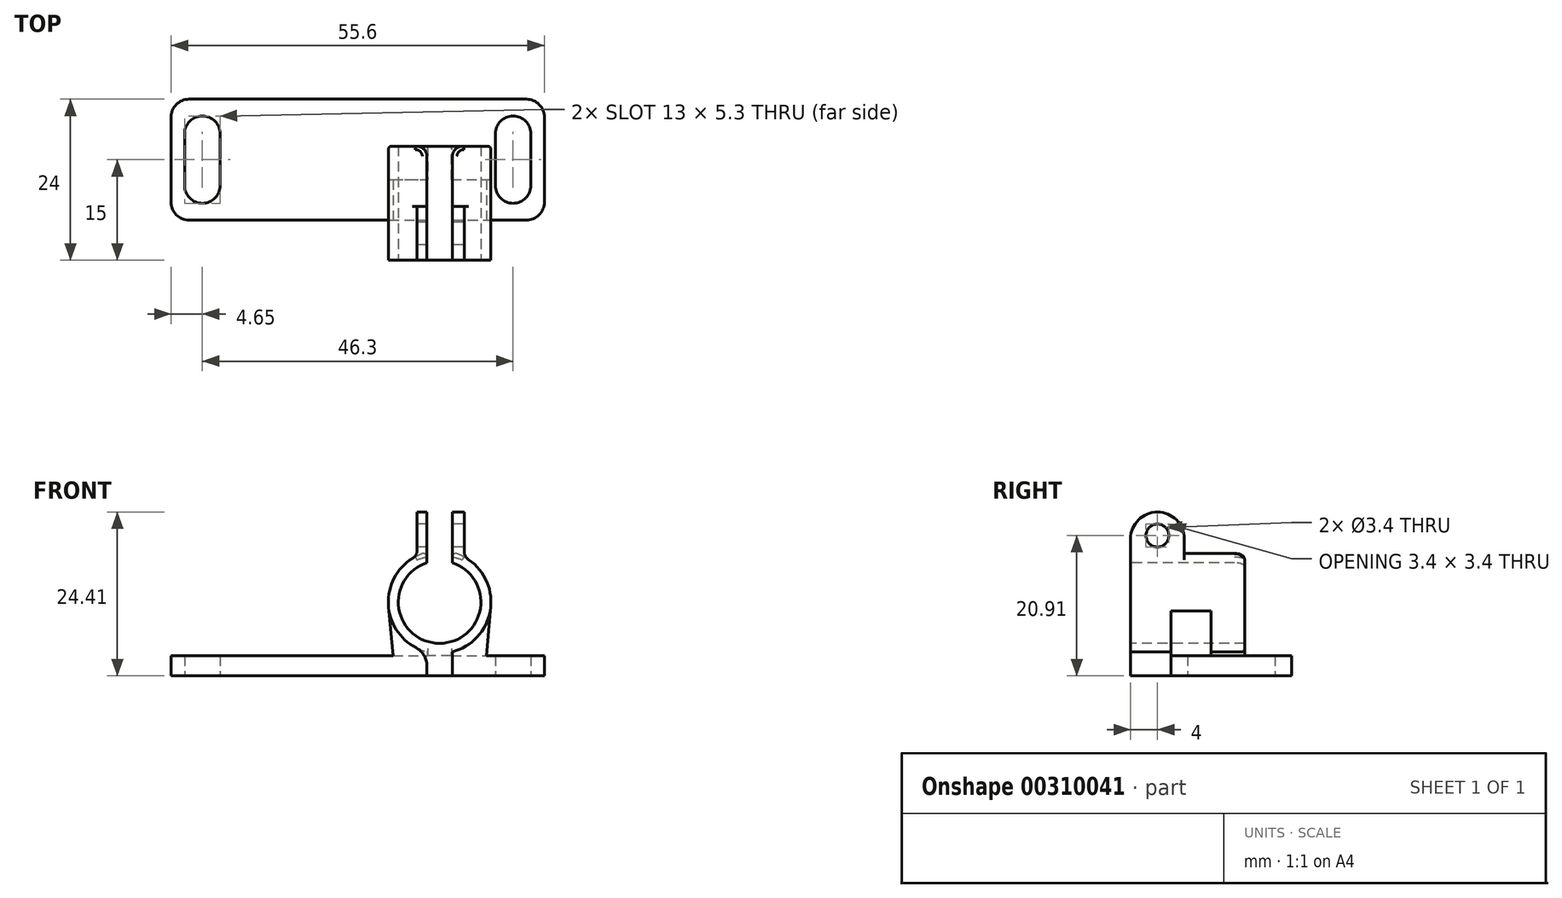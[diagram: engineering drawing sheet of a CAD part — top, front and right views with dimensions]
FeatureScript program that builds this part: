
annotation { "Feature Type Name" : "Feature", "Feature Type Description" : "" }
export const myFeature = defineFeature(function(context is Context, id is Id, definition is map)
    precondition{}
    {
        {
            var Q0;
            Q0=qCreatedBy(makeId("Top.planeOp"),FACE);
            var sketch = newSketch(context, id + "F0", { "sketchPlane" : qUnion([Q0])});
            skLineSegment(sketch, "E0.bottom", {"start": v(2.65, 0) * mm, "end": v(2.65, 0) * mm});
            skLineSegment(sketch, "E0.top", {"start": v(2.65, 13) * mm, "end": v(2.65, 13) * mm});
            skLineSegment(sketch, "E0.left", {"start": v(0, 2.65) * mm, "end": v(0, 10.35) * mm});
            skLineSegment(sketch, "E0.right", {"start": v(5.3, 2.65) * mm, "end": v(5.3, 10.35) * mm});
            skLineSegment(sketch, "E1.bottom", {"start": v(48.95, 0) * mm, "end": v(48.95, 0) * mm});
            skLineSegment(sketch, "E1.top", {"start": v(48.95, 13) * mm, "end": v(48.95, 13) * mm});
            skLineSegment(sketch, "E1.left", {"start": v(46.3, 2.65) * mm, "end": v(46.3, 10.35) * mm});
            skLineSegment(sketch, "E1.right", {"start": v(51.6, 2.65) * mm, "end": v(51.6, 10.35) * mm});
            skPoint(sketch, "E2.visualSharp", {"position": v(0, 13) * mm});
            skArc(sketch, "E2.filletArc", {"start": v(2.65, 13) * mm, "mid": v(0.78, 12.22) * mm, "end": v(0, 10.35) * mm});
            skPoint(sketch, "E3.visualSharp", {"position": v(5.3, 13) * mm});
            skArc(sketch, "E3.filletArc", {"start": v(5.3, 10.35) * mm, "mid": v(4.52, 12.22) * mm, "end": v(2.65, 13) * mm});
            skPoint(sketch, "E4.visualSharp", {"position": v(0, 0) * mm});
            skArc(sketch, "E4.filletArc", {"start": v(0, 2.65) * mm, "mid": v(0.78, 0.78) * mm, "end": v(2.65, 0) * mm});
            skPoint(sketch, "E5.visualSharp", {"position": v(5.3, 0) * mm});
            skArc(sketch, "E5.filletArc", {"start": v(2.65, 0) * mm, "mid": v(4.52, 0.78) * mm, "end": v(5.3, 2.65) * mm});
            skPoint(sketch, "E6.visualSharp", {"position": v(46.3, 13) * mm});
            skArc(sketch, "E6.filletArc", {"start": v(48.95, 13) * mm, "mid": v(47.08, 12.22) * mm, "end": v(46.3, 10.35) * mm});
            skPoint(sketch, "E7.visualSharp", {"position": v(51.6, 13) * mm});
            skArc(sketch, "E7.filletArc", {"start": v(51.6, 10.35) * mm, "mid": v(50.82, 12.22) * mm, "end": v(48.95, 13) * mm});
            skPoint(sketch, "E8.visualSharp", {"position": v(51.6, 0) * mm});
            skArc(sketch, "E8.filletArc", {"start": v(48.95, 0) * mm, "mid": v(50.82, 0.78) * mm, "end": v(51.6, 2.65) * mm});
            skPoint(sketch, "E9.visualSharp", {"position": v(46.3, 0) * mm});
            skArc(sketch, "E9.filletArc", {"start": v(46.3, 2.65) * mm, "mid": v(47.08, 0.78) * mm, "end": v(48.95, 0) * mm});
            skLineSegment(sketch, "E10.bottom", {"start": v(0.65, -2.5) * mm, "end": v(50.95, -2.5) * mm});
            skLineSegment(sketch, "E10.top", {"start": v(0.65, 15.5) * mm, "end": v(50.95, 15.5) * mm});
            skLineSegment(sketch, "E10.left", {"start": v(-2, 0.15) * mm, "end": v(-2, 12.85) * mm});
            skLineSegment(sketch, "E10.right", {"start": v(53.6, 0.15) * mm, "end": v(53.6, 12.85) * mm});
            skPoint(sketch, "E11.visualSharp", {"position": v(-2, 15.5) * mm});
            skArc(sketch, "E11.filletArc", {"start": v(0.65, 15.5) * mm, "mid": v(-1.22, 14.72) * mm, "end": v(-2, 12.85) * mm});
            skPoint(sketch, "E12.visualSharp", {"position": v(53.6, 15.5) * mm});
            skArc(sketch, "E12.filletArc", {"start": v(53.6, 12.85) * mm, "mid": v(52.82, 14.72) * mm, "end": v(50.95, 15.5) * mm});
            skPoint(sketch, "E13.visualSharp", {"position": v(53.6, -2.5) * mm});
            skArc(sketch, "E13.filletArc", {"start": v(50.95, -2.5) * mm, "mid": v(52.82, -1.72) * mm, "end": v(53.6, 0.15) * mm});
            skPoint(sketch, "E14.visualSharp", {"position": v(-2, -2.5) * mm});
            skArc(sketch, "E14.filletArc", {"start": v(-2, 0.15) * mm, "mid": v(-1.22, -1.72) * mm, "end": v(0.65, -2.5) * mm});
            skSolve(sketch);
        }
        {
            var Q0;
            Q0=makeQuery(id+"F0.imprint","IMPRINT",FACE,{"disambiguationData":[TD([[makeQuery(id+"F0.imprint","IMPRINT",EDGE,{"derivedFrom":sQuery(id+"F0.wireOp",EDGE,"E0.left")}),1.0]])]});
            extrude(context, id + "F1", {"entities" : qUnion([Q0]), "depth" : 3 * mm});
        }
        {
            var Q0;
            Q0=qCreatedBy(makeId("Front.planeOp"),FACE);
            var sketch = newSketch(context, id + "F2", { "sketchPlane" : qUnion([Q0])});
            skArc(sketch, "E15", {"start": v(36.1, 16.85) * mm, "mid": v(38, 4.85) * mm, "end": v(39.9, 16.85) * mm});
            skArc(sketch, "E16", {"start": v(36.1, 18.41) * mm, "mid": v(38, 3.35) * mm, "end": v(39.9, 18.41) * mm});
            skLineSegment(sketch, "E17", {"start": v(39.9, 18.41) * mm, "end": v(39.9, 16.85) * mm});
            skLineSegment(sketch, "E18", {"start": v(36.1, 18.41) * mm, "end": v(36.1, 16.85) * mm});
            skSolve(sketch);
        }
        {
            var Q0;
            Q0=makeQuery(id+"F2.imprint","IMPRINT",FACE,{"disambiguationData":[TD([[makeQuery(id+"F2.imprint","IMPRINT",EDGE,{"derivedFrom":sQuery(id+"F2.wireOp",EDGE,"E15")}),-1.0]])]});
            extrude(context, id + "F3", {"entities" : qUnion([Q0]), "endBound" : BoundingType.SYMMETRIC, "oppositeDirection" : true, "depth" : 17 * mm});
        }
        {
            var Q0;
            Q0=makeQuery(id+"F1.opExtrude","SWEPT_FACE",FACE,{"disambiguationData":[OSD([sQuery(id+"F0.wireOp",EDGE,"E10.bottom")])]});
            var sketch = newSketch(context, id + "F4", { "sketchPlane" : qUnion([Q0])});
            skArc(sketch, "E19", {"start": v(30.35, 11) * mm, "mid": v(38, 3.35) * mm, "end": v(45.65, 11) * mm});
            skLineSegment(sketch, "E20", {"start": v(30.35, 11) * mm, "end": v(31.05, 3) * mm});
            skLineSegment(sketch, "E21", {"start": v(31.05, 3) * mm, "end": v(44.95, 3) * mm});
            skLineSegment(sketch, "E22", {"start": v(44.95, 3) * mm, "end": v(45.65, 11) * mm});
            skSolve(sketch);
        }
        {
            var Q0;
            Q0=makeQuery(id+"F4.imprint","IMPRINT",FACE,{"disambiguationData":[TD([[makeQuery(id+"F4.imprint","IMPRINT",EDGE,{"derivedFrom":sQuery(id+"F4.wireOp",EDGE,"E19")}),-1.0]])]});
            extrude(context, id + "F5", {"entities" : qUnion([Q0]), "operationType" : NewBodyOperationType.ADD, "oppositeDirection" : true, "depth" : 6 * mm});
        }
        {
            var Q0;
            Q0=makeQuery(id+"F3.opExtrude","CAP_FACE",FACE,{"disambiguationData":[OSD([sQuery(id+"F2.wireOp",EDGE,"E15"),sQuery(id+"F2.wireOp",EDGE,"E16"),sQuery(id+"F2.wireOp",EDGE,"E17"),sQuery(id+"F2.wireOp",EDGE,"E18")])],"isStart":false});
            var sketch = newSketch(context, id + "F6", { "sketchPlane" : qUnion([Q0])});
            skLineSegment(sketch, "E23", {"start": v(-39.75, 3.7) * mm, "end": v(-39.75, 0) * mm});
            skLineSegment(sketch, "E24", {"start": v(-39.75, 0) * mm, "end": v(-36.1, 0) * mm});
            skLineSegment(sketch, "E25", {"start": v(-36.1, 0) * mm, "end": v(-36.25, 3.7) * mm});
            skArc(sketch, "E26", {"start": v(-39.75, 3.7) * mm, "mid": v(-38, 3.5) * mm, "end": v(-36.25, 3.7) * mm});
            skSolve(sketch);
        }
        {
            var Q0;
            {var subQ0=sQuery(id+"F6.wireOp",EDGE,"E24");Q0=makeQuery(id+"F6.imprint","IMPRINT",FACE,{"disambiguationData":[TD([[makeQuery(id+"F6.imprint","IMPRINT",EDGE,{"derivedFrom":subQ0}),1.0]])]});}
            extrude(context, id + "F7", {"entities" : qUnion([Q0]), "operationType" : NewBodyOperationType.ADD, "oppositeDirection" : true, "depth" : 10 * mm});
        }
        {
            var Q0;
            Q0=makeQuery(id+"F3.opExtrude","CAP_FACE",FACE,{"disambiguationData":[OSD([sQuery(id+"F2.wireOp",EDGE,"E15"),sQuery(id+"F2.wireOp",EDGE,"E16"),sQuery(id+"F2.wireOp",EDGE,"E17"),sQuery(id+"F2.wireOp",EDGE,"E18")])],"isStart":true});
            var sketch = newSketch(context, id + "F8", { "sketchPlane" : qUnion([Q0])});
            skLineSegment(sketch, "E27", {"start": v(36.1, 3.59) * mm, "end": v(36.1, 0) * mm});
            skLineSegment(sketch, "E28", {"start": v(36.1, 0) * mm, "end": v(39.9, 0) * mm});
            skLineSegment(sketch, "E29", {"start": v(39.9, 0) * mm, "end": v(39.9, 3.59) * mm});
            skLineSegment(sketch, "E30", {"start": v(39.9, 3.59) * mm, "end": v(36.1, 3.59) * mm});
            skSolve(sketch);
        }
        {
            var Q0;
            {var subQ0=sQuery(id+"F8.wireOp",EDGE,"E27");Q0=makeQuery(id+"F8.imprint","IMPRINT",FACE,{"disambiguationData":[TD([[makeQuery(id+"F8.imprint","IMPRINT",EDGE,{"derivedFrom":subQ0}),1.0]])]});}
            extrude(context, id + "F9", {"entities" : qUnion([Q0]), "operationType" : NewBodyOperationType.ADD, "endBound" : BoundingType.UP_TO_NEXT, "oppositeDirection" : true, "depth" : 25 * mm});
        }
        {
            var Q0;
            Q0=makeQuery(id+"F9.opExtrude","SWEPT_EDGE",EDGE,{"disambiguationData":[OSD([sQuery(id+"F2.wireOp",EDGE,"E16"),sQuery(id+"F8.wireOp",EDGE,"E29"),sQuery(id+"F8.wireOp",EDGE,"E30")])]});
            var Q1;
            Q1=makeQuery(id+"F9.opExtrude","SWEPT_EDGE",EDGE,{"disambiguationData":[OSD([sQuery(id+"F2.wireOp",EDGE,"E16"),sQuery(id+"F8.wireOp",EDGE,"E27"),sQuery(id+"F8.wireOp",EDGE,"E30")])]});
            fillet(context, id + "F10", {"entities" : qUnion([Q0, Q1]), "radius" : 3 * mm, "tangentPropagation" : true, "allowEdgeOverflow" : false});
        }
        {
            var Q0;
            Q0=makeQuery(id+"F3.opExtrude","SWEPT_FACE",FACE,{"disambiguationData":[OSD([sQuery(id+"F2.wireOp",EDGE,"E17")])]});
            cPlane(context, id + "F11", {"entities" : qUnion([Q0]), "cplaneType" : CPlaneType.OFFSET, "offset" : 1.75 * mm, "width" : 150 * mm, "height" : 150 * mm});
        }
        {
            var Q0;
            Q0=qCreatedBy(id+"F11.planeOp",FACE);
            var sketch = newSketch(context, id + "F12", { "sketchPlane" : qUnion([Q0])});
            skCircle(sketch, "E31", {"center": v(4.5, 20.91) * mm, "radius": 1.7 * mm});
            skLineSegment(sketch, "E32", {"start": v(0.5, 16.91) * mm, "end": v(0.5, 20.41) * mm});
            skLineSegment(sketch, "E33", {"start": v(4.5, 24.41) * mm, "end": v(4.5, 24.41) * mm});
            skLineSegment(sketch, "E34", {"start": v(8.5, 20.41) * mm, "end": v(8.5, 16.91) * mm});
            skLineSegment(sketch, "E35", {"start": v(0.5, 16.91) * mm, "end": v(8.5, 16.91) * mm});
            skPoint(sketch, "E36.visualSharp", {"position": v(0.5, 24.41) * mm});
            skArc(sketch, "E36.filletArc", {"start": v(4.5, 24.41) * mm, "mid": v(1.67, 23.24) * mm, "end": v(0.5, 20.41) * mm});
            skPoint(sketch, "E37.visualSharp", {"position": v(8.5, 24.41) * mm});
            skArc(sketch, "E37.filletArc", {"start": v(8.5, 20.41) * mm, "mid": v(7.33, 23.24) * mm, "end": v(4.5, 24.41) * mm});
            skSolve(sketch);
        }
        {
            var Q0;
            Q0=makeQuery(id+"F12.imprint","IMPRINT",FACE,{"disambiguationData":[TD([[makeQuery(id+"F12.imprint","IMPRINT",EDGE,{"derivedFrom":sQuery(id+"F12.wireOp",EDGE,"E31")}),-1.0]])]});
            extrude(context, id + "F13", {"entities" : qUnion([Q0]), "operationType" : NewBodyOperationType.ADD, "endBound" : BoundingType.SYMMETRIC, "oppositeDirection" : true, "depth" : 7 * mm});
        }
        {
            var Q0;
            Q0=makeQuery(id+"F13.opExtrude","CAP_EDGE",EDGE,{"disambiguationData":[OSD([sQuery(id+"F12.wireOp",EDGE,"E35")])],"isStart":true});
            var Q1;
            {var subQ1=sQuery(id+"F2.wireOp",EDGE,"E16");var subQ6=sQuery(id+"F2.wireOp",EDGE,"E18");Q1=makeQuery(id+"F13.boolean.opBoolean","INTERSECT",EDGE,{"derivedFrom":[makeQuery(id+"F9.boolean.opBoolean","SPLIT",FACE,{"disambiguationData":[TD([makeQuery(id+"F3.opExtrude","SWEPT_FACE",FACE,{"disambiguationData":[OSD([subQ6])]})])],"derivedFrom":makeQuery(id+"F3.opExtrude","SWEPT_FACE",FACE,{"disambiguationData":[OSD([subQ1])]})}),makeQuery(id+"F13.opExtrude","CAP_FACE",FACE,{"disambiguationData":[OSD([sQuery(id+"F12.wireOp",EDGE,"E31"),sQuery(id+"F12.wireOp",EDGE,"E32"),sQuery(id+"F12.wireOp",EDGE,"E34"),sQuery(id+"F12.wireOp",EDGE,"E35"),sQuery(id+"F12.wireOp",EDGE,"E36.filletArc"),sQuery(id+"F12.wireOp",EDGE,"E37.filletArc")])],"isStart":true})]});}
            var Q2;
            {var subQ1=sQuery(id+"F2.wireOp",EDGE,"E16");var subQ8=sQuery(id+"F2.wireOp",EDGE,"E17");Q2=makeQuery(id+"F13.boolean.opBoolean","INTERSECT",EDGE,{"derivedFrom":[makeQuery(id+"F9.boolean.opBoolean","SPLIT",FACE,{"disambiguationData":[TD([makeQuery(id+"F3.opExtrude","SWEPT_FACE",FACE,{"disambiguationData":[OSD([subQ8])]})])],"derivedFrom":makeQuery(id+"F3.opExtrude","SWEPT_FACE",FACE,{"disambiguationData":[OSD([subQ1])]})}),makeQuery(id+"F13.opExtrude","CAP_FACE",FACE,{"disambiguationData":[OSD([sQuery(id+"F12.wireOp",EDGE,"E31"),sQuery(id+"F12.wireOp",EDGE,"E32"),sQuery(id+"F12.wireOp",EDGE,"E34"),sQuery(id+"F12.wireOp",EDGE,"E35"),sQuery(id+"F12.wireOp",EDGE,"E36.filletArc"),sQuery(id+"F12.wireOp",EDGE,"E37.filletArc")])],"isStart":false})]});}
            fillet(context, id + "F14", {"entities" : qUnion([Q0, Q1, Q2]), "radius" : 1.5 * mm, "tangentPropagation" : true, "allowEdgeOverflow" : false});
        }
        {
            var Q0;
            Q0=makeQuery(id+"F13.opExtrude","SWEPT_FACE",FACE,{"disambiguationData":[OSD([sQuery(id+"F12.wireOp",EDGE,"E35")])]});
            var sketch = newSketch(context, id + "F15", { "sketchPlane" : qUnion([Q0])});
            skLineSegment(sketch, "E38.bottom", {"start": v(36.1, 8.5) * mm, "end": v(39.9, 8.5) * mm});
            skLineSegment(sketch, "E38.top", {"start": v(36.1, 0.5) * mm, "end": v(39.9, 0.5) * mm});
            skLineSegment(sketch, "E38.left", {"start": v(36.1, 8.5) * mm, "end": v(36.1, 0.5) * mm});
            skLineSegment(sketch, "E38.right", {"start": v(39.9, 8.5) * mm, "end": v(39.9, 0.5) * mm});
            skSolve(sketch);
        }
        {
            var Q0;
            Q0=makeQuery(id+"F15.imprint","IMPRINT",FACE,{"disambiguationData":[TD([[makeQuery(id+"F15.imprint","IMPRINT",EDGE,{"derivedFrom":sQuery(id+"F15.wireOp",EDGE,"E38.bottom")}),1.0]])]});
            extrude(context, id + "F16", {"entities" : qUnion([Q0]), "operationType" : NewBodyOperationType.REMOVE, "oppositeDirection" : true, "depth" : 25 * mm});
        }
        {
            var Q0;
            Q0=makeQuery(id+"F3.opExtrude","CAP_EDGE",EDGE,{"disambiguationData":[OSD([sQuery(id+"F2.wireOp",EDGE,"E18")])],"isStart":false});
            var Q1;
            Q1=makeQuery(id+"F3.opExtrude","CAP_EDGE",EDGE,{"disambiguationData":[OSD([sQuery(id+"F2.wireOp",EDGE,"E17")])],"isStart":false});
            fillet(context, id + "F17", {"entities" : qUnion([Q0, Q1]), "radius" : 1.5 * mm, "tangentPropagation" : true, "allowEdgeOverflow" : false});
        }
        {
            var Q0;
            Q0=makeQuery(id+"F3.opExtrude","SWEPT_EDGE",EDGE,{"disambiguationData":[OSD([sQuery(id+"F2.wireOp",EDGE,"E16"),sQuery(id+"F2.wireOp",EDGE,"E18")])]});
            var Q1;
            Q1=makeQuery(id+"F3.opExtrude","SWEPT_EDGE",EDGE,{"disambiguationData":[OSD([sQuery(id+"F2.wireOp",EDGE,"E16"),sQuery(id+"F2.wireOp",EDGE,"E17")])]});
            fillet(context, id + "F18", {"entities" : qUnion([Q0, Q1]), "radius" : .5 * mm, "tangentPropagation" : true, "allowEdgeOverflow" : false});
        }
    });
